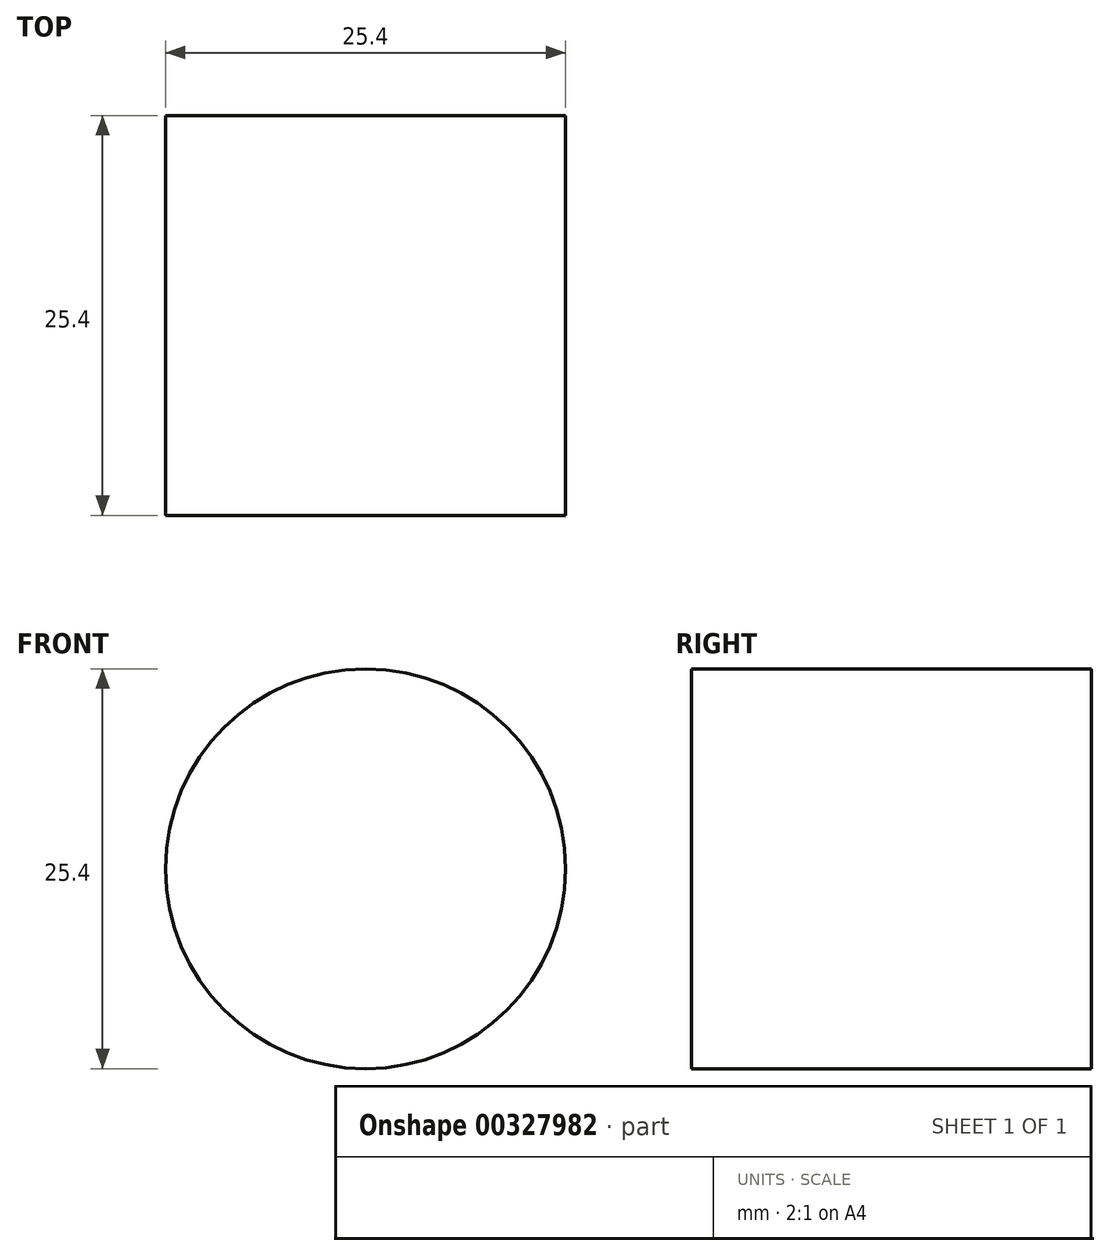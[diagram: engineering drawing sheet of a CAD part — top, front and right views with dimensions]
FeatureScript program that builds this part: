
annotation { "Feature Type Name" : "Feature", "Feature Type Description" : "" }
export const myFeature = defineFeature(function(context is Context, id is Id, definition is map)
    precondition{}
    {
        {
            var Q0;
            Q0=qCreatedBy(makeId("Front.planeOp"),FACE);
            var sketch = newSketch(context, id + "F0", { "sketchPlane" : qUnion([Q0])});
            skCircle(sketch, "E0", {"center": v(0, 0) * mm, "radius": 12.7 * mm});
            skSolve(sketch);
        }
        {
            var Q0;
            Q0=makeQuery(id+"F0.imprint","IMPRINT",FACE,{"disambiguationData":[TD([[makeQuery(id+"F0.imprint","IMPRINT",EDGE,{"derivedFrom":sQuery(id+"F0.wireOp",EDGE,"E0")}),1.0]])]});
            extrude(context, id + "F1", {"entities" : qUnion([Q0]), "depth" : 25.4 * mm});
        }
    });
